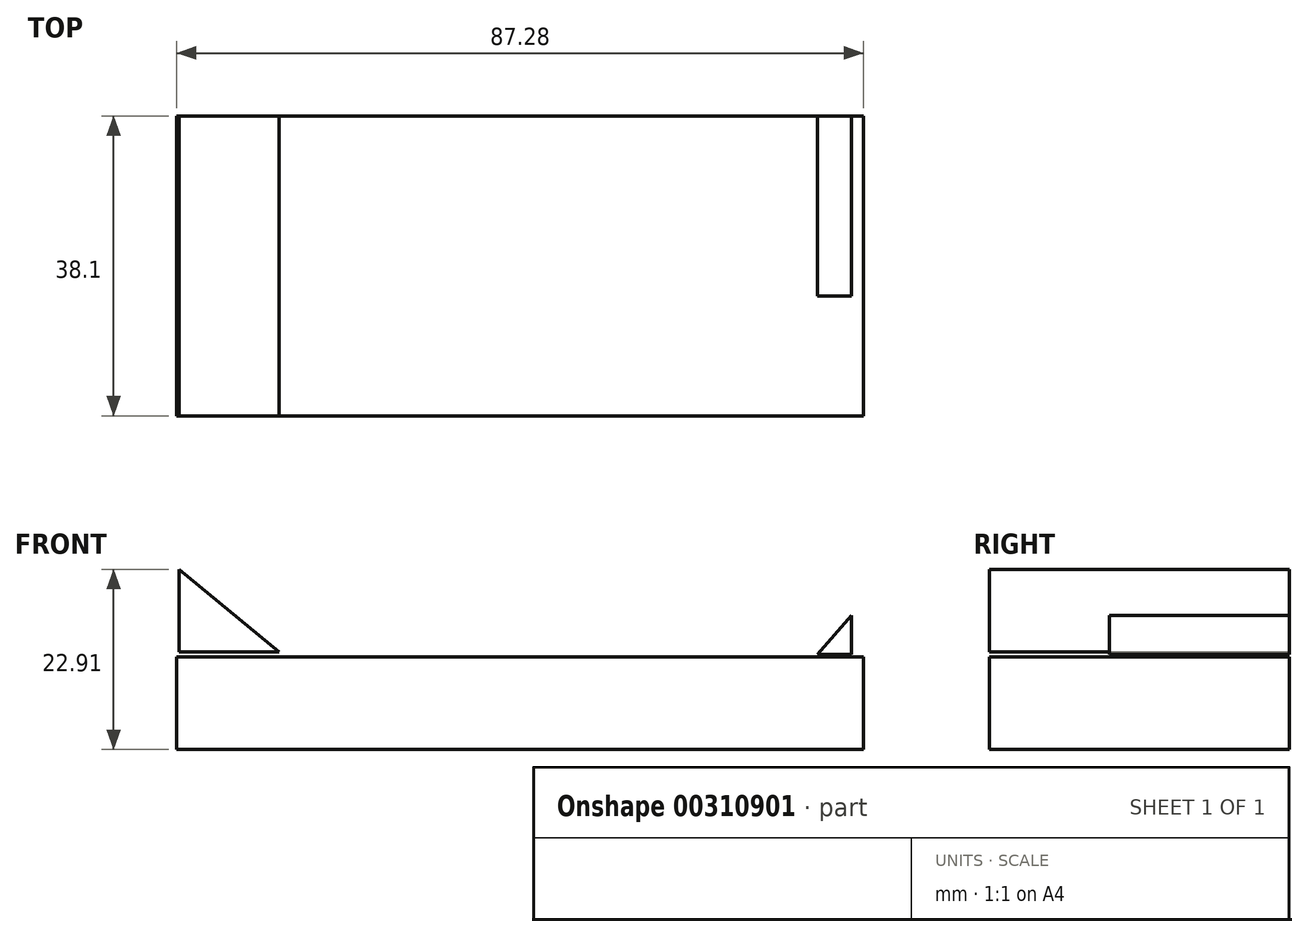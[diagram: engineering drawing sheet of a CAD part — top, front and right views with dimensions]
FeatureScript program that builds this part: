
annotation { "Feature Type Name" : "Feature", "Feature Type Description" : "" }
export const myFeature = defineFeature(function(context is Context, id is Id, definition is map)
    precondition{}
    {
        {
            var Q0;
            Q0=qCreatedBy(makeId("Front.planeOp"),FACE);
            var sketch = newSketch(context, id + "F0", { "sketchPlane" : qUnion([Q0])});
            skLineSegment(sketch, "E0", {"start": v(-49.52, -49.99) * mm, "end": v(37.76, -49.99) * mm});
            skLineSegment(sketch, "E1", {"start": v(37.76, -49.99) * mm, "end": v(37.76, -38.23) * mm});
            skLineSegment(sketch, "E2", {"start": v(37.76, -38.23) * mm, "end": v(-49.52, -38.23) * mm});
            skLineSegment(sketch, "E3", {"start": v(-49.52, -38.23) * mm, "end": v(-49.52, -49.99) * mm});
            skSolve(sketch);
        }
        {
            var Q0;
            Q0=qCreatedBy(makeId("Front.planeOp"),FACE);
            var sketch = newSketch(context, id + "F1", { "sketchPlane" : qUnion([Q0])});
            skLineSegment(sketch, "E4", {"start": v(-49.21, -27.08) * mm, "end": v(-49.21, -37.6) * mm});
            skLineSegment(sketch, "E5", {"start": v(-49.21, -37.6) * mm, "end": v(-36.52, -37.6) * mm});
            skLineSegment(sketch, "E6", {"start": v(-36.52, -37.6) * mm, "end": v(-49.21, -27.08) * mm});
            skSolve(sketch);
        }
        {
            var Q0;
            Q0=qCreatedBy(makeId("Front.planeOp"),FACE);
            var sketch = newSketch(context, id + "F2", { "sketchPlane" : qUnion([Q0])});
            skLineSegment(sketch, "E7", {"start": v(31.88, -37.92) * mm, "end": v(36.21, -32.96) * mm});
            skLineSegment(sketch, "E8", {"start": v(31.88, -37.92) * mm, "end": v(36.21, -37.92) * mm});
            skLineSegment(sketch, "E9", {"start": v(36.21, -37.92) * mm, "end": v(36.21, -32.96) * mm});
            skSolve(sketch);
        }
        {
            var Q0;
            Q0 = qSketchRegion(id + "F0", true);
            extrude(context, id + "F3", {"entities" : qUnion([Q0]), "depth" : 38.1 * mm});
        }
        {
            var Q0;
            Q0 = qSketchRegion(id + "F1", true);
            extrude(context, id + "F4", {"entities" : qUnion([Q0]), "depth" : 38.1 * mm});
        }
        {
            var Q0;
            Q0 = qSketchRegion(id + "F2", true);
            extrude(context, id + "F5", {"entities" : qUnion([Q0]), "depth" : 22.86 * mm});
        }
    });
